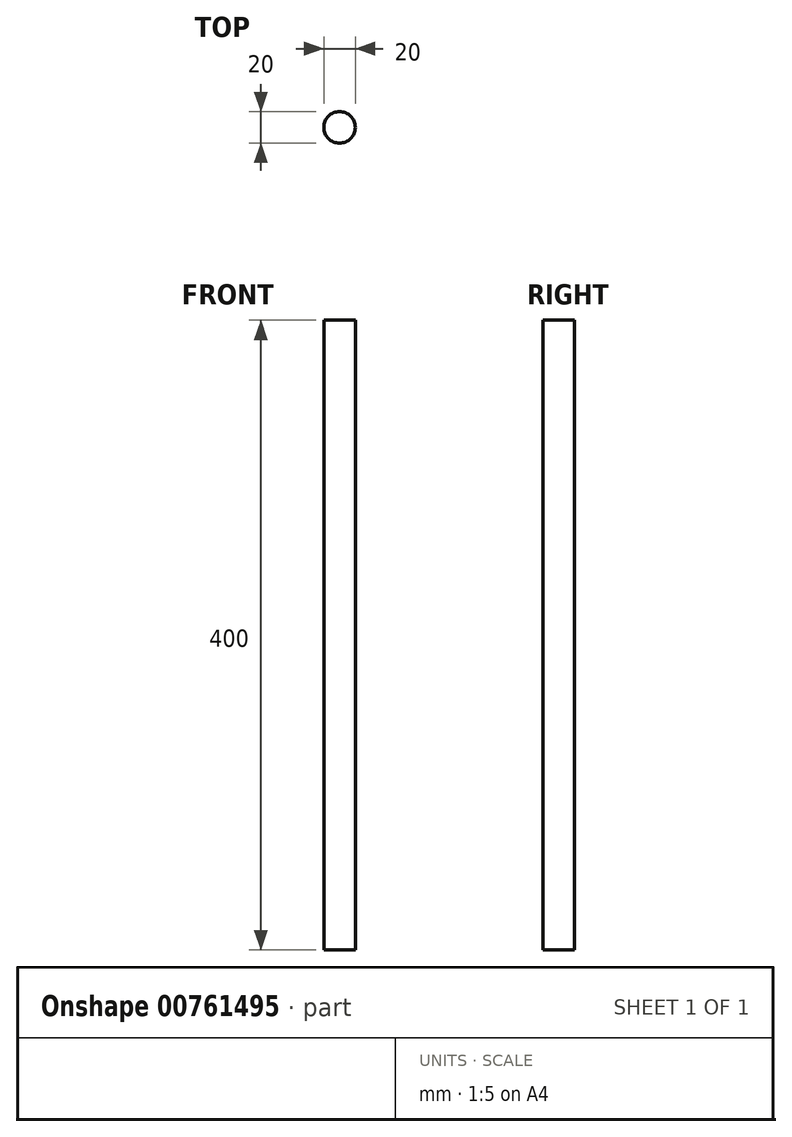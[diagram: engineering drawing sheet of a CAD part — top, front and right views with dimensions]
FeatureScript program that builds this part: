
annotation { "Feature Type Name" : "Feature", "Feature Type Description" : "" }
export const myFeature = defineFeature(function(context is Context, id is Id, definition is map)
    precondition{}
    {
        {
            var Q0;
            Q0=qCreatedBy(makeId("Top.planeOp"),FACE);
            var sketch = newSketch(context, id + "F0", { "sketchPlane" : qUnion([Q0])});
            skCircle(sketch, "E0", {"center": v(0, 0) * mm, "radius": 10 * mm});
            skSolve(sketch);
        }
        {
            var Q0;
            Q0 = qSketchRegion(id + "F0", true);
            extrude(context, id + "F1", {"entities" : qUnion([Q0]), "depth" : 400 * mm, "offsetDistance" : 25 * mm});
        }
    });
